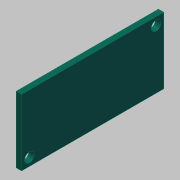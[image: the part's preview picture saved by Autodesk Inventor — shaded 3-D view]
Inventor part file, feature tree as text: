
AUTODESK INVENTOR PART (.ipt)
format: ipt  version: 2012 (Build 160160000, 160)  size: 93,184 bytes
history: native  units: mm (DEFAULTED — no unit token found)
features: sketch x2, extrude x1, hole x1
ambient origin geometry x8: Origin, YZ Plane, XZ Plane, XY Plane, X Axis, Y Axis, Z Axis, Center Point
bodies: Solid1 (feature_tree)
feature tree (4):
  extrude  "Extrusion1"  Depth=21.3mm
  hole  "Hole1"  [1 undecoded]
  sketch  "Sketch1"  dims[d0=45.7mm d1=21.3mm]
  sketch  "Sketch2"  dims[d2=1.75mm d3=0.0mm d4=2.5mm d5=2.5mm d6=2.5mm d7=2.5mm d8=3.1mm d9=6.0mm d10=4.0mm d11=2.0mm d12=14.3117mm d13=8.0mm d14=20.594885mm]
note: 1 required parameter value undecoded (feature->parameter linkage not recoverable at this tier; creation-order binding heuristic only, values carry confidence <= 0.55)
